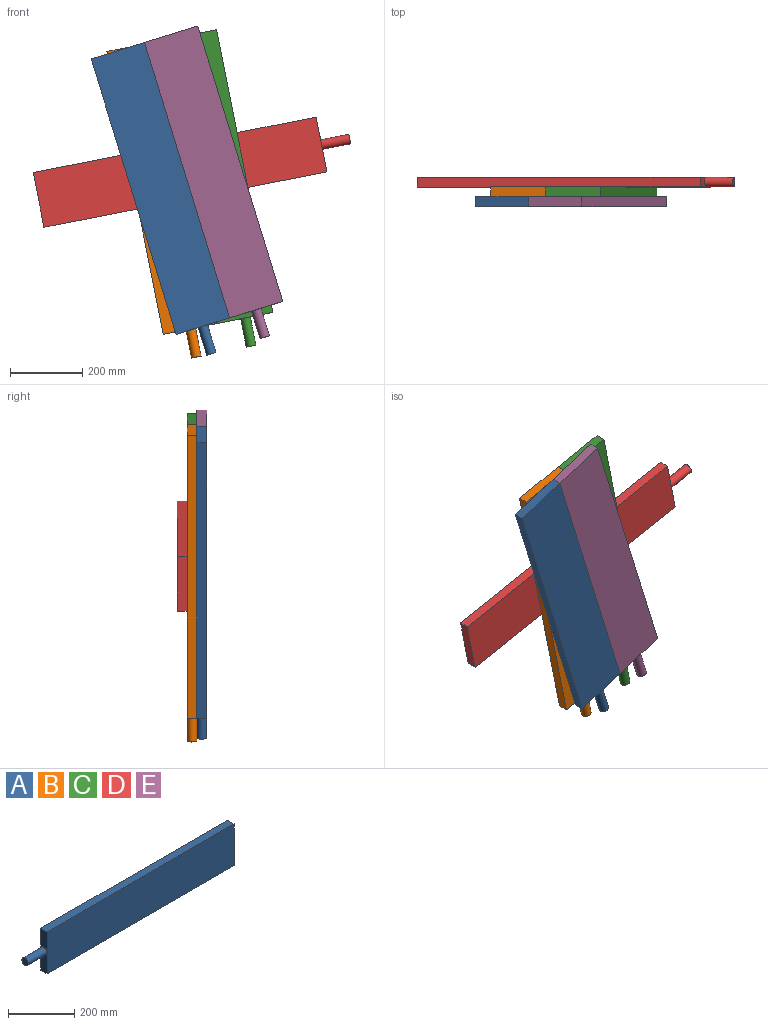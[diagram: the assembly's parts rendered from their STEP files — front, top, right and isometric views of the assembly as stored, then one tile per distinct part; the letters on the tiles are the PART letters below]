
ASSEMBLY  parts=5 mates=8
PART A: 9 faces, bbox 880x27x155 mm
  f0: plane 77.5x27mm, normal (-1,0,0), area 1806.2mm2, adj f1,f2,f4,f7
  f1: plane 800x27mm, normal (0,0,1), area 21600mm2, adj f0,f2,f4,f5
  f2: plane 800x155mm, normal (0,-1,0), area 124000mm2, adj f0,f1,f3,f5,f6
  f3: plane 800x27mm, normal (0,0,-1), area 21600mm2, adj f2,f4,f5,f6
  f4: plane 800x155mm, normal (0,1,0), area 124000mm2, adj f0,f1,f3,f5,f6
  f5: plane 155x27mm, normal (1,0,0), area 4185mm2, adj f1,f2,f3,f4
  f6: plane 77.5x27mm, normal (-1,0,0), area 1806.2mm2, adj f2,f3,f4,f7
  f7: cylinder r=13.5mm len=80mm, axis (1,0,0), area 6785.8mm2, adj f0,f6,f8
  f8: plane 27x27mm, normal (-1,0,0), area 572.6mm2, adj f7
PART B: same geometry as A
PART C: same geometry as A
PART D: same geometry as A
PART E: same geometry as A
PLACE A rot(axis=(0,-1,0),107.1deg) t=(-325.79,185.42,-264.3)mm
PLACE B rot(axis=(0,-1,0),101.3deg) t=(-317.84,212.42,-269.28)mm
PLACE C rot(axis=(0,-1,0),101.3deg) t=(-165.83,212.42,-238.96)mm
PLACE D rot(axis=(0,1,0),168.9deg) t=(-359.9,239.42,-166.13)mm
PLACE E rot(axis=(0,-1,0),107.1deg) t=(-177.68,185.42,-218.61)mm
MATE parallel A.f4 <-> E.f2  axis (0,1,0) through (-399.85,260.89,-287.15)mm
MATE planar C.f1 <-> B.f3  axis (-0.98,0,-0.2) through (-317.84,274.39,-269.28)mm
MATE planar E.f1 <-> A.f3  axis (-0.96,0,-0.29) through (-325.79,247.39,-264.3)mm
MATE parallel C.f4 <-> A.f2  axis (0,1,0) through (-241.83,287.89,-254.12)mm
MATE parallel E.f4 <-> B.f2  axis (0,1,0) through (-251.74,260.89,-241.45)mm
MATE planar A.f4 <-> C.f2  axis (0,1,0) through (-325.79,260.89,-264.3)mm
MATE parallel D.f2 <-> B.f4  axis (0,-1,0) through (-345.03,287.89,-242.19)mm
MATE parallel E.f1 <-> A.f3  axis (-0.96,0,-0.29) through (-325.79,247.39,-264.3)mm
